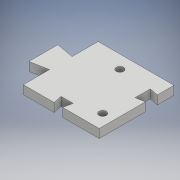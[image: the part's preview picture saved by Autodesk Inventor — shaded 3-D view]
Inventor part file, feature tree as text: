
AUTODESK INVENTOR PART (.ipt)
format: ipt  version: 2017 (Build 210142000, 142)  size: 427,008 bytes
history: native  units: mm
features: extrude x36, sketch x36, shell x1
ambient origin geometry x8: Origin, YZ Plane, XZ Plane, XY Plane, X Axis, Y Axis, Z Axis, Center Point
bodies: Solid1 (feature_tree)
feature tree (73):
  extrude  "Extrusion1"  Depth=37.0mm
  shell  "Shell1"  Thickness=20.0mm
  extrude  "Extrusion2"  Depth=55.0mm
  extrude  "Extrusion3"  TaperAngle=0.0deg  [1 undecoded]
  extrude  "Extrusion4"  Depth=5.0mm
  extrude  "Extrusion5"  TaperAngle=0.0deg  [1 undecoded]
  extrude  "Extrusion6"  Depth=10.0mm TaperAngle=0.0deg
  extrude  "Extrusion7"  Depth=15.0mm TaperAngle=0.0deg
  extrude  "Extrusion9"  Depth=8.5mm
  extrude  "Extrusion10"  Depth=15.0mm TaperAngle=0.0deg
  extrude  "Extrusion11"  Depth=35.46mm
  extrude  "Extrusion12"  Depth=15.0mm TaperAngle=0.0deg
  extrude  "Extrusion13"  Depth=4.5mm
  extrude  "Extrusion14"  Depth=15.0mm TaperAngle=0.0deg
  extrude  "Extrusion15"  Depth=8.5mm
  extrude  "Extrusion16"  Depth=15.0mm TaperAngle=0.0deg
  extrude  "Extrusion17"  Depth=28.505mm
  extrude  "Extrusion18"  Depth=15.0mm TaperAngle=0.0deg
  extrude  "Extrusion19"  Depth=36.0mm
  extrude  "Extrusion20"  Depth=15.0mm TaperAngle=0.0deg
  extrude  "Extrusion23"  Depth=5.0mm
  extrude  "Extrusion21"  Depth=4.1656mm
  extrude  "Extrusion22"  Depth=35.46mm
  extrude  "Extrusion24"  Depth=10.0mm
  extrude  "Extrusion25"  Depth=10.0mm TaperAngle=0.0deg
  extrude  "Extrusion26"  Depth=2.583mm TaperAngle=0.0deg
  extrude  "Extrusion27"  Depth=2.583mm TaperAngle=0.0deg
  extrude  "Extrusion28"  Depth=100.0mm TaperAngle=0.0deg
  extrude  "Extrusion29"  Depth=5.0mm
  extrude  "Extrusion30"  Depth=1.0mm
  extrude  "Extrusion31"  Depth=5.0mm
  extrude  "Extrusion32"  Depth=4.1656mm
  extrude  "Extrusion33"  Depth=6.161mm
  extrude  "Extrusion34"  Depth=4.1656mm
  extrude  "Extrusion35"  Depth=15.906mm
  extrude  "Extrusion36"  Depth=22.5mm TaperAngle=0.0deg
  extrude  "Extrusion37"  Depth=5.0mm TaperAngle=0.0deg
  sketch  "Sketch1"  dims[d0=35.0mm d1=37.0mm d2=20.0mm]
  sketch  "Sketch2"  dims[d3=11.0mm d4=55.0mm]
  sketch  "Sketch3"  dims[d5=26.0mm d6=0.0mm]
  sketch  "Sketch4"  dims[d7=50.0mm d8=0.0mm d9=5.0mm]
  sketch  "Sketch5"  dims[d10=17.0mm d11=0.0mm]
  sketch  "Sketch6"  dims[d12=11.0mm d13=10.0mm d14=0.0mm]
  sketch  "Sketch7"  dims[d15=15.0mm d16=0.0mm d17=15.0mm d18=0.0mm]
  sketch  "Sketch13"  dims[d19=4.1656mm d20=8.5mm]
  sketch  "Sketch14"  dims[d21=11.5mm d22=15.0mm d23=0.0mm]
  sketch  "Sketch15"  dims[d24=4.1656mm d25=35.46mm]
  sketch  "Sketch16"  dims[d26=23.505mm d27=15.0mm d28=0.0mm]
  sketch  "Sketch17"  dims[d29=4.1656mm d30=4.5mm]
  sketch  "Sketch18"  dims[d31=14.0mm d32=15.0mm d33=0.0mm]
  sketch  "Sketch20"  dims[d41=4.1656mm d42=8.5mm]
  sketch  "Sketch21"  dims[d43=11.5mm d44=15.0mm d45=0.0mm]
  sketch  "Sketch22"  dims[d46=4.1656mm d47=28.505mm]
  sketch  "Sketch23"  dims[d48=35.46mm d49=15.0mm d50=0.0mm]
  sketch  "Sketch24"  dims[d51=4.1656mm d52=36.0mm]
  sketch  "Sketch25"  dims[d53=4.5mm d54=15.0mm d55=0.0mm]
  sketch  "Sketch26"  dims[d56=5.0mm d57=50.0mm]
  sketch  "Sketch27"  dims[d58=21.0mm d59=0.0mm d60=4.1656mm]
  sketch  "Sketch28"  dims[d61=23.505mm d62=35.46mm]
  sketch  "Sketch29"  dims[d63=10.0mm d64=0.0mm d65=4.1656mm]
  sketch  "Sketch30"  dims[d67=36.0mm d68=10.0mm d69=0.0mm]
  sketch  "Sketch31"  dims[d70=4.5mm d71=2.583mm d72=0.0mm]
  sketch  "Sketch33"  dims[d73=2.583mm d74=0.0mm d75=2.583mm d76=0.0mm]
  sketch  "Sketch34"  dims[d77=6.917mm d78=100.0mm d79=0.0mm]
  sketch  "Sketch35"  dims[d80=5.0mm d81=5.0mm]
  sketch  "Sketch36"  dims[d83=1.0mm d84=1.0mm]
  sketch  "Sketch38"  dims[d88=22.5mm d89=0.0mm d90=4.1656mm]
  sketch  "Sketch40"  dims[d93=25.0mm d94=0.0mm d95=4.1656mm]
  sketch  "Sketch41"  dims[d96=2.702mm d97=15.906mm]
  sketch  "Sketch44"  dims[d102=2.5mm d103=22.5mm d104=0.0mm d105=9.0mm d106=4.0mm d107=5.0mm d108=0.0mm d109=30.0mm d110=0.0mm d111=4.1656mm d112=6.083mm d113=4.0mm d114=30.0mm d115=0.0mm d116=30.0mm d117=0.0mm d118=30.0mm d119=0.0mm d120=30.0mm d121=0.0mm d122=10.0mm d123=0.0mm d124=8.6943mm d125=13.962634mm d126=29.670597mm d127=5.0mm d130=5.0mm d131=34.389mm d132=10.0mm d133=0.0mm d134=10.0mm d135=0.0mm d136=8.6943mm d137=13.962634mm d138=29.670597mm d139=5.0mm d140=0.0mm d141=8.694mm d142=42.0mm d143=0.0mm d144=37.0mm d145=0.0mm d146=5.0mm d147=27.0mm d148=0.0mm d149=8.6943mm d150=13.962634mm d151=29.670597mm d152=5.0mm d153=0.0mm d154=9.187mm d155=5.0mm d156=0.0mm d157=15.0mm d158=15.0mm d159=13.083mm d160=13.962634mm d161=13.962634mm d162=10.0mm d163=5.0mm d164=0.0mm]
  sketch  "Sketch37"  dims[d85=100.0mm d86=0.0mm d87=5.0mm]
  sketch  "Sketch39"  dims[d91=5.851mm d92=6.161mm]
  sketch  "Sketch43"  dims[d98=25.0mm d99=0.0mm d100=22.5mm d101=0.0mm]
note: 2 required parameter values undecoded (feature->parameter linkage not recoverable at this tier; creation-order binding heuristic only, values carry confidence <= 0.55)
